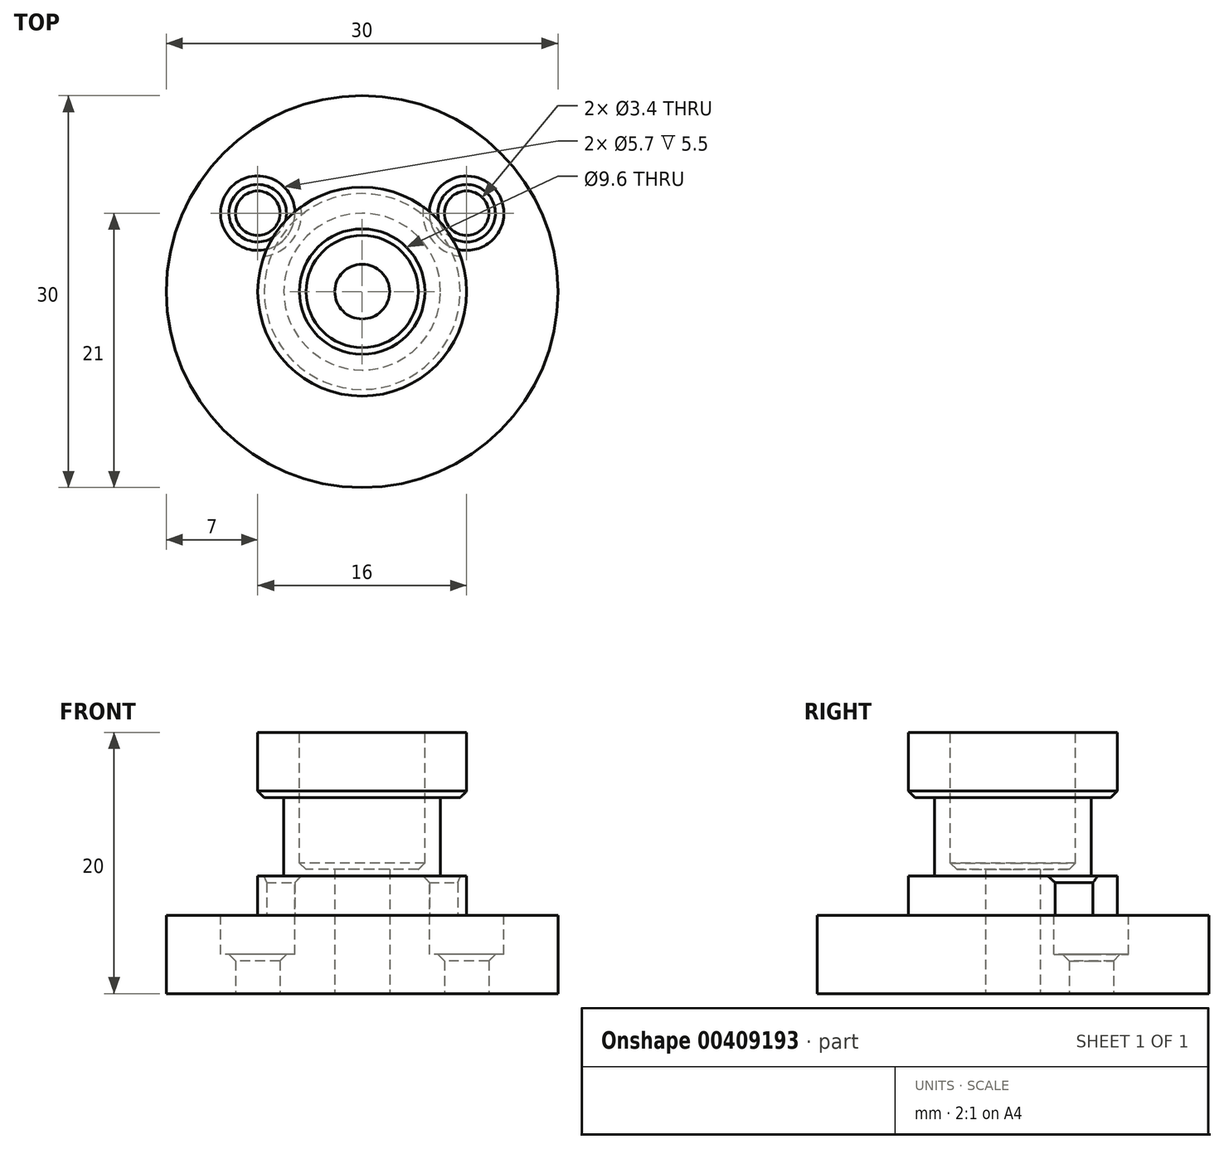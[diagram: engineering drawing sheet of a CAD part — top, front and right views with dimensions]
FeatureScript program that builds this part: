
annotation { "Feature Type Name" : "Feature", "Feature Type Description" : "" }
export const myFeature = defineFeature(function(context is Context, id is Id, definition is map)
    precondition{}
    {
        {
            var Q0;
            Q0=qCreatedBy(makeId("Top.planeOp"),FACE);
            var sketch = newSketch(context, id + "F0", { "sketchPlane" : qUnion([Q0])});
            skCircle(sketch, "E0", {"center": v(0, 0) * mm, "radius": 10 * mm, "construction": true});
            skCircle(sketch, "E1", {"center": v(0, 0) * mm, "radius": 15 * mm});
            skLineSegment(sketch, "E2", {"start": v(-8, 6) * mm, "end": v(8, 6) * mm, "construction": true});
            skCircle(sketch, "E3", {"center": v(-8, 6) * mm, "radius": 1.7 * mm});
            skCircle(sketch, "E4", {"center": v(8, 6) * mm, "radius": 1.7 * mm});
            skCircle(sketch, "E5", {"center": v(0, 0) * mm, "radius": 2.1 * mm});
            skSolve(sketch);
        }
        {
            var Q0;
            Q0=makeQuery(id+"F0.imprint","IMPRINT",FACE,{"disambiguationData":[TD([[makeQuery(id+"F0.imprint","IMPRINT",EDGE,{"derivedFrom":sQuery(id+"F0.wireOp",EDGE,"E1")}),1.0]])]});
            extrude(context, id + "F1", {"entities" : qUnion([Q0]), "depth" : 6 * mm});
        }
        {
            var Q0;
            Q0=makeQuery(id+"F1.opExtrude","CAP_FACE",FACE,{"disambiguationData":[OSD([sQuery(id+"F0.wireOp",EDGE,"E1"),sQuery(id+"F0.wireOp",EDGE,"E3"),sQuery(id+"F0.wireOp",EDGE,"E4"),sQuery(id+"F0.wireOp",EDGE,"E5")])],"isStart":false});
            var sketch = newSketch(context, id + "F2", { "sketchPlane" : qUnion([Q0])});
            skCircle(sketch, "E6", {"center": v(-8, 6) * mm, "radius": 2.85 * mm});
            skCircle(sketch, "E7", {"center": v(8, 6) * mm, "radius": 2.85 * mm});
            skSolve(sketch);
        }
        {
            var Q0;
            Q0=qSketchRegion(id+"F2",true);
            extrude(context, id + "F3", {"entities" : qUnion([Q0]), "operationType" : NewBodyOperationType.REMOVE, "oppositeDirection" : true, "depth" : 3 * mm});
        }
        {
            var Q0;
            Q0=makeQuery(id+"F1.opExtrude","CAP_FACE",FACE,{"disambiguationData":[OSD([sQuery(id+"F0.wireOp",EDGE,"E1"),sQuery(id+"F0.wireOp",EDGE,"E3"),sQuery(id+"F0.wireOp",EDGE,"E4"),sQuery(id+"F0.wireOp",EDGE,"E5")])],"isStart":false});
            var sketch = newSketch(context, id + "F4", { "sketchPlane" : qUnion([Q0])});
            skCircle(sketch, "E8", {"center": v(0, 0) * mm, "radius": 8 * mm});
            skSolve(sketch);
        }
        {
            var Q0;
            Q0=makeQuery(id+"F4.imprint","IMPRINT",FACE,{"disambiguationData":[TD([[makeQuery(id+"F4.imprint","IMPRINT",EDGE,{"derivedFrom":makeQuery(id+"F1.opExtrude","CAP_EDGE",EDGE,{"disambiguationData":[OSD([sQuery(id+"F0.wireOp",EDGE,"E5")])],"isStart":false})}),-1.0]])]});
            extrude(context, id + "F5", {"entities" : qUnion([Q0]), "operationType" : NewBodyOperationType.ADD, "depth" : 3 * mm});
        }
        {
            var Q0;
            Q0=makeQuery(id+"F5.opExtrude","CAP_FACE",FACE,{"disambiguationData":[OSD([sQuery(id+"F0.wireOp",EDGE,"E5"),sQuery(id+"F2.wireOp",EDGE,"E6"),sQuery(id+"F2.wireOp",EDGE,"E7"),sQuery(id+"F4.wireOp",EDGE,"E8")])],"isStart":false});
            var sketch = newSketch(context, id + "F6", { "sketchPlane" : qUnion([Q0])});
            skCircle(sketch, "E9", {"center": v(0, 0) * mm, "radius": 6 * mm});
            skSolve(sketch);
        }
        {
            var Q0;
            Q0=makeQuery(id+"F6.imprint","IMPRINT",FACE,{"disambiguationData":[TD([[makeQuery(id+"F6.imprint","IMPRINT",EDGE,{"derivedFrom":sQuery(id+"F6.wireOp",EDGE,"E9")}),1.0]])]});
            extrude(context, id + "F7", {"entities" : qUnion([Q0]), "operationType" : NewBodyOperationType.ADD, "depth" : 6 * mm});
        }
        {
            var Q0;
            Q0=makeQuery(id+"F7.opExtrude","CAP_FACE",FACE,{"disambiguationData":[OSD([sQuery(id+"F0.wireOp",EDGE,"E5"),sQuery(id+"F6.wireOp",EDGE,"E9")])],"isStart":false});
            var sketch = newSketch(context, id + "F8", { "sketchPlane" : qUnion([Q0])});
            skCircle(sketch, "E10", {"center": v(0, 0) * mm, "radius": 8 * mm});
            skSolve(sketch);
        }
        {
            var Q0;
            Q0=makeQuery(id+"F8.imprint","IMPRINT",FACE,{"disambiguationData":[TD([[makeQuery(id+"F8.imprint","IMPRINT",EDGE,{"derivedFrom":makeQuery(id+"F7.opExtrude","CAP_EDGE",EDGE,{"disambiguationData":[OSD([sQuery(id+"F6.wireOp",EDGE,"E9")])],"isStart":false})}),1.0]])]});
            var Q1;
            Q1=makeQuery(id+"F8.imprint","IMPRINT",FACE,{"disambiguationData":[TD([[makeQuery(id+"F8.imprint","IMPRINT",EDGE,{"derivedFrom":sQuery(id+"F8.wireOp",EDGE,"E10")}),1.0]])]});
            extrude(context, id + "F9", {"entities" : qUnion([Q0, Q1]), "operationType" : NewBodyOperationType.ADD, "depth" : 5 * mm});
        }
        {
            var Q0;
            Q0=makeQuery(id+"F9.opExtrude","CAP_FACE",FACE,{"disambiguationData":[OSD([sQuery(id+"F0.wireOp",EDGE,"E5"),sQuery(id+"F8.wireOp",EDGE,"E10")])],"isStart":false});
            var sketch = newSketch(context, id + "F10", { "sketchPlane" : qUnion([Q0])});
            skCircle(sketch, "E11", {"center": v(0, 0) * mm, "radius": 4.8 * mm});
            skSolve(sketch);
        }
        {
            var Q0;
            Q0=makeQuery(id+"F10.imprint","IMPRINT",FACE,{"disambiguationData":[TD([[makeQuery(id+"F10.imprint","IMPRINT",EDGE,{"derivedFrom":sQuery(id+"F10.wireOp",EDGE,"E11")}),1.0]])]});
            extrude(context, id + "F11", {"entities" : qUnion([Q0]), "operationType" : NewBodyOperationType.REMOVE, "oppositeDirection" : true, "depth" : 10.5 * mm});
        }
        {
            var Q0;
            Q0=makeQuery(id+"F11.boolean.opBoolean","COPY",EDGE,{"derivedFrom":makeQuery(id+"F11.opExtrude","CAP_EDGE",EDGE,{"disambiguationData":[OSD([sQuery(id+"F10.wireOp",EDGE,"E11")])],"isStart":true})});
            var Q1;
            Q1=makeQuery(id+"F11.boolean.opBoolean","COPY",EDGE,{"derivedFrom":makeQuery(id+"F11.opExtrude","CAP_EDGE",EDGE,{"disambiguationData":[OSD([sQuery(id+"F0.wireOp",EDGE,"E5")])],"isStart":false})});
            var Q2;
            Q2=makeQuery(id+"F11.boolean.opBoolean","COPY",EDGE,{"derivedFrom":makeQuery(id+"F11.opExtrude","CAP_EDGE",EDGE,{"disambiguationData":[OSD([sQuery(id+"F10.wireOp",EDGE,"E11")])],"isStart":false})});
            var Q3;
            Q3=makeQuery(id+"F3.boolean.opBoolean","INTERSECT",EDGE,{"derivedFrom":[makeQuery(id+"F1.opExtrude","SWEPT_FACE",FACE,{"disambiguationData":[OSD([sQuery(id+"F0.wireOp",EDGE,"E3")])]}),makeQuery(id+"F3.opExtrude","CAP_FACE",FACE,{"disambiguationData":[OSD([sQuery(id+"F2.wireOp",EDGE,"E6")])],"isStart":false})]});
            var Q4;
            Q4=makeQuery(id+"F3.boolean.opBoolean","COPY",EDGE,{"derivedFrom":makeQuery(id+"F3.opExtrude","CAP_EDGE",EDGE,{"disambiguationData":[OSD([sQuery(id+"F2.wireOp",EDGE,"E6")])],"isStart":true})});
            var Q5;
            Q5=makeQuery(id+"F3.boolean.opBoolean","INTERSECT",EDGE,{"derivedFrom":[makeQuery(id+"F1.opExtrude","SWEPT_FACE",FACE,{"disambiguationData":[OSD([sQuery(id+"F0.wireOp",EDGE,"E4")])]}),makeQuery(id+"F3.opExtrude","CAP_FACE",FACE,{"disambiguationData":[OSD([sQuery(id+"F2.wireOp",EDGE,"E7")])],"isStart":false})]});
            var Q6;
            Q6=makeQuery(id+"F3.boolean.opBoolean","COPY",EDGE,{"derivedFrom":makeQuery(id+"F3.opExtrude","CAP_EDGE",EDGE,{"disambiguationData":[OSD([sQuery(id+"F2.wireOp",EDGE,"E7")])],"isStart":true})});
            var Q7;
            Q7=makeQuery(id+"F5.opExtrude","CAP_EDGE",EDGE,{"disambiguationData":[OSD([sQuery(id+"F2.wireOp",EDGE,"E7")])],"isStart":false});
            var Q8;
            Q8=makeQuery(id+"F5.opExtrude","CAP_EDGE",EDGE,{"disambiguationData":[OSD([sQuery(id+"F2.wireOp",EDGE,"E6")])],"isStart":false});
            var Q9;
            Q9=makeQuery(id+"F9.opExtrude","CAP_EDGE",EDGE,{"disambiguationData":[OSD([sQuery(id+"F8.wireOp",EDGE,"E10")])],"isStart":true});
            var Q10;
            {var subQ0=sQuery(id+"F4.wireOp",EDGE,"E8");Q10=makeQuery(id+"F5.opExtrude","CAP_EDGE",EDGE,{"disambiguationData":[OSD([subQ0]),TDD([makeQuery(id+"F4.imprint","IMPRINT",EDGE,{"disambiguationData":[TD([[makeQuery(id+"F4.imprint","INTERSECT",VERTEX,{"disambiguationData":[OD(1.0)],"derivedFrom":[makeQuery(id+"F3.boolean.opBoolean","COPY",EDGE,{"derivedFrom":makeQuery(id+"F3.opExtrude","CAP_EDGE",EDGE,{"disambiguationData":[OSD([sQuery(id+"F2.wireOp",EDGE,"E7")])],"isStart":true})}),subQ0]}),1.0]])],"derivedFrom":subQ0})])],"isStart":false});}
            var Q11;
            {var subQ0=sQuery(id+"F4.wireOp",EDGE,"E8");Q11=makeQuery(id+"F5.opExtrude","CAP_EDGE",EDGE,{"disambiguationData":[OSD([subQ0]),TDD([makeQuery(id+"F4.imprint","IMPRINT",EDGE,{"disambiguationData":[TD([[makeQuery(id+"F4.imprint","INTERSECT",VERTEX,{"disambiguationData":[OD(0.0)],"derivedFrom":[makeQuery(id+"F3.boolean.opBoolean","COPY",EDGE,{"derivedFrom":makeQuery(id+"F3.opExtrude","CAP_EDGE",EDGE,{"disambiguationData":[OSD([sQuery(id+"F2.wireOp",EDGE,"E7")])],"isStart":true})}),subQ0]}),-1.0]])],"derivedFrom":subQ0})])],"isStart":false});}
            chamfer(context, id + "F12", {"entities" : qUnion([Q0, Q1, Q2, Q3, Q4, Q5, Q6, Q7, Q8, Q9, Q10, Q11]), "width" : 0.5 * mm, "tangentPropagation" : true});
        }
    });
